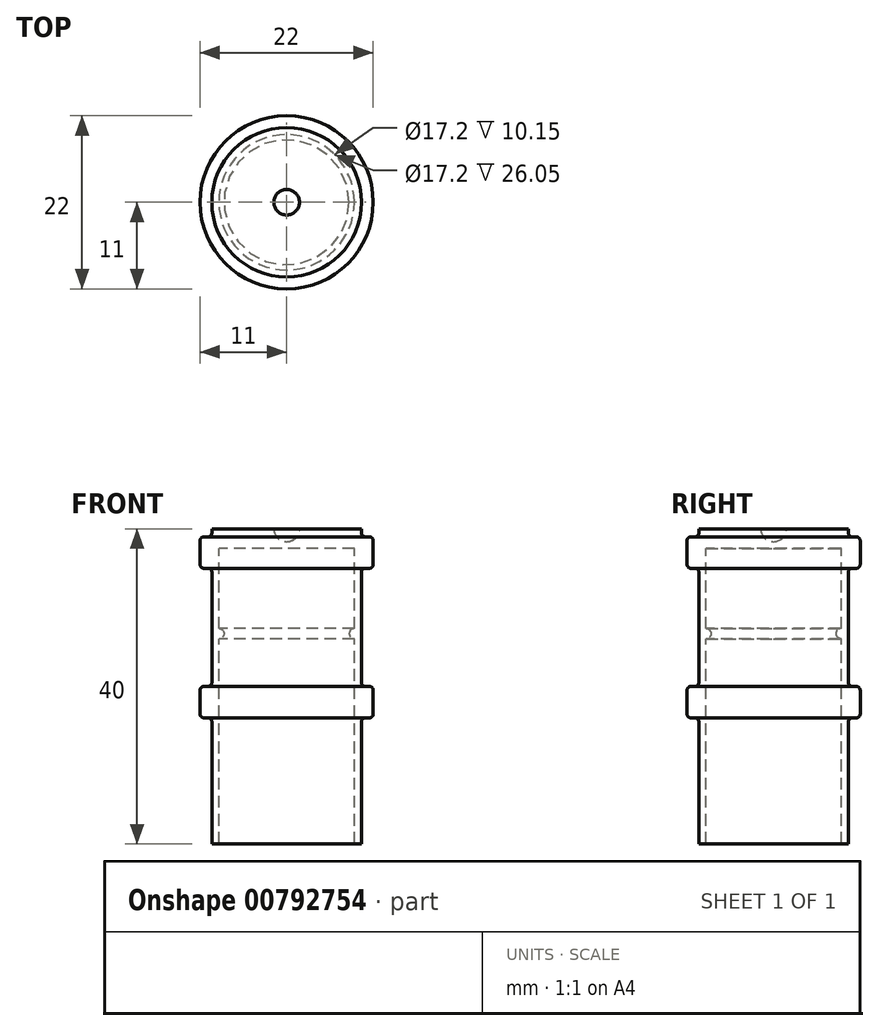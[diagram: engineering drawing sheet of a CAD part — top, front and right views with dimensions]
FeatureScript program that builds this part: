
annotation { "Feature Type Name" : "Feature", "Feature Type Description" : "" }
export const myFeature = defineFeature(function(context is Context, id is Id, definition is map)
    precondition{}
    {
        {
            var Q0;
            Q0=qCreatedBy(makeId("Front.planeOp"),FACE);
            var sketch = newSketch(context, id + "F0", { "sketchPlane" : qUnion([Q0])});
            skLineSegment(sketch, "E0", {"start": v(1.63, 28.94) * mm, "end": v(9.5, 28.94) * mm});
            skLineSegment(sketch, "E1", {"start": v(9.5, 23.44) * mm, "end": v(9.5, 9.44) * mm});
            skLineSegment(sketch, "E2", {"start": v(10, 27.94) * mm, "end": v(10.5, 27.94) * mm});
            skLineSegment(sketch, "E3", {"start": v(11, 27.44) * mm, "end": v(11, 24.44) * mm});
            skLineSegment(sketch, "E4", {"start": v(10.5, 23.94) * mm, "end": v(10, 23.94) * mm});
            skLineSegment(sketch, "E5", {"start": v(10, 8.94) * mm, "end": v(10.5, 8.94) * mm});
            skLineSegment(sketch, "E6", {"start": v(11, 8.44) * mm, "end": v(11, 5.44) * mm});
            skLineSegment(sketch, "E7", {"start": v(10.5, 4.94) * mm, "end": v(10, 4.94) * mm});
            skLineSegment(sketch, "E8", {"start": v(0, 28.94) * mm, "end": v(0, 26.44) * mm});
            skLineSegment(sketch, "E9", {"start": v(0, 26.44) * mm, "end": v(8.6, 26.44) * mm});
            skLineSegment(sketch, "E10", {"start": v(8.6, 26.44) * mm, "end": v(8.6, -11.06) * mm});
            skLineSegment(sketch, "E11", {"start": v(9.5, -11.06) * mm, "end": v(8.6, -11.06) * mm});
            skArc(sketch, "E12", {"start": v(0, 27.32) * mm, "mid": v(1.15, 27.8) * mm, "end": v(1.63, 28.94) * mm});
            skArc(sketch, "E13", {"start": v(8.6, 16.3) * mm, "mid": v(7.95, 15.64) * mm, "end": v(8.6, 15) * mm});
            skPoint(sketch, "E14.newPointB", {"position": v(9.5, 23.94) * mm});
            skArc(sketch, "E14.filletArc", {"start": v(10, 23.94) * mm, "mid": v(9.65, 23.8) * mm, "end": v(9.5, 23.44) * mm});
            skLineSegment(sketch, "E15", {"start": v(9.5, 28.44) * mm, "end": v(9.5, 28.94) * mm});
            skPoint(sketch, "E16.visualSharp", {"position": v(9.5, 27.94) * mm});
            skArc(sketch, "E16.filletArc", {"start": v(9.5, 28.44) * mm, "mid": v(9.65, 28.09) * mm, "end": v(10, 27.94) * mm});
            skPoint(sketch, "E17.visualSharp", {"position": v(11, 27.94) * mm});
            skArc(sketch, "E17.filletArc", {"start": v(11, 27.44) * mm, "mid": v(10.85, 27.8) * mm, "end": v(10.5, 27.94) * mm});
            skPoint(sketch, "E18.visualSharp", {"position": v(11, 23.94) * mm});
            skArc(sketch, "E18.filletArc", {"start": v(10.5, 23.94) * mm, "mid": v(10.85, 24.09) * mm, "end": v(11, 24.44) * mm});
            skPoint(sketch, "E19.newPointA", {"position": v(9.5, -11.06) * mm});
            skArc(sketch, "E19.filletArc", {"start": v(9.5, 9.44) * mm, "mid": v(9.65, 9.09) * mm, "end": v(10, 8.94) * mm});
            skPoint(sketch, "E20.visualSharp", {"position": v(11, 8.94) * mm});
            skArc(sketch, "E20.filletArc", {"start": v(11, 8.44) * mm, "mid": v(10.85, 8.8) * mm, "end": v(10.5, 8.94) * mm});
            skPoint(sketch, "E21.visualSharp", {"position": v(11, 4.94) * mm});
            skArc(sketch, "E21.filletArc", {"start": v(10.5, 4.94) * mm, "mid": v(10.85, 5.09) * mm, "end": v(11, 5.44) * mm});
            skLineSegment(sketch, "E22", {"start": v(9.5, 4.44) * mm, "end": v(9.5, -11.06) * mm});
            skPoint(sketch, "E23.visualSharp", {"position": v(9.5, 4.94) * mm});
            skArc(sketch, "E23.filletArc", {"start": v(10, 4.94) * mm, "mid": v(9.65, 4.8) * mm, "end": v(9.5, 4.44) * mm});
            skSolve(sketch);
        }
        {
            var Q0;
            Q0 = qSketchRegion(id + "F0", true);
            var Q1;
            Q1=sQuery(id+"F0.wireOp",EDGE,"E8");
            revolve(context, id + "F1", {"surfaceOperationType" : NewSurfaceOperationType.NEW, "entities" : qUnion([Q0]), "axis" : qUnion([Q1]), "revolveType" : RevolveType.FULL});
        }
    });
